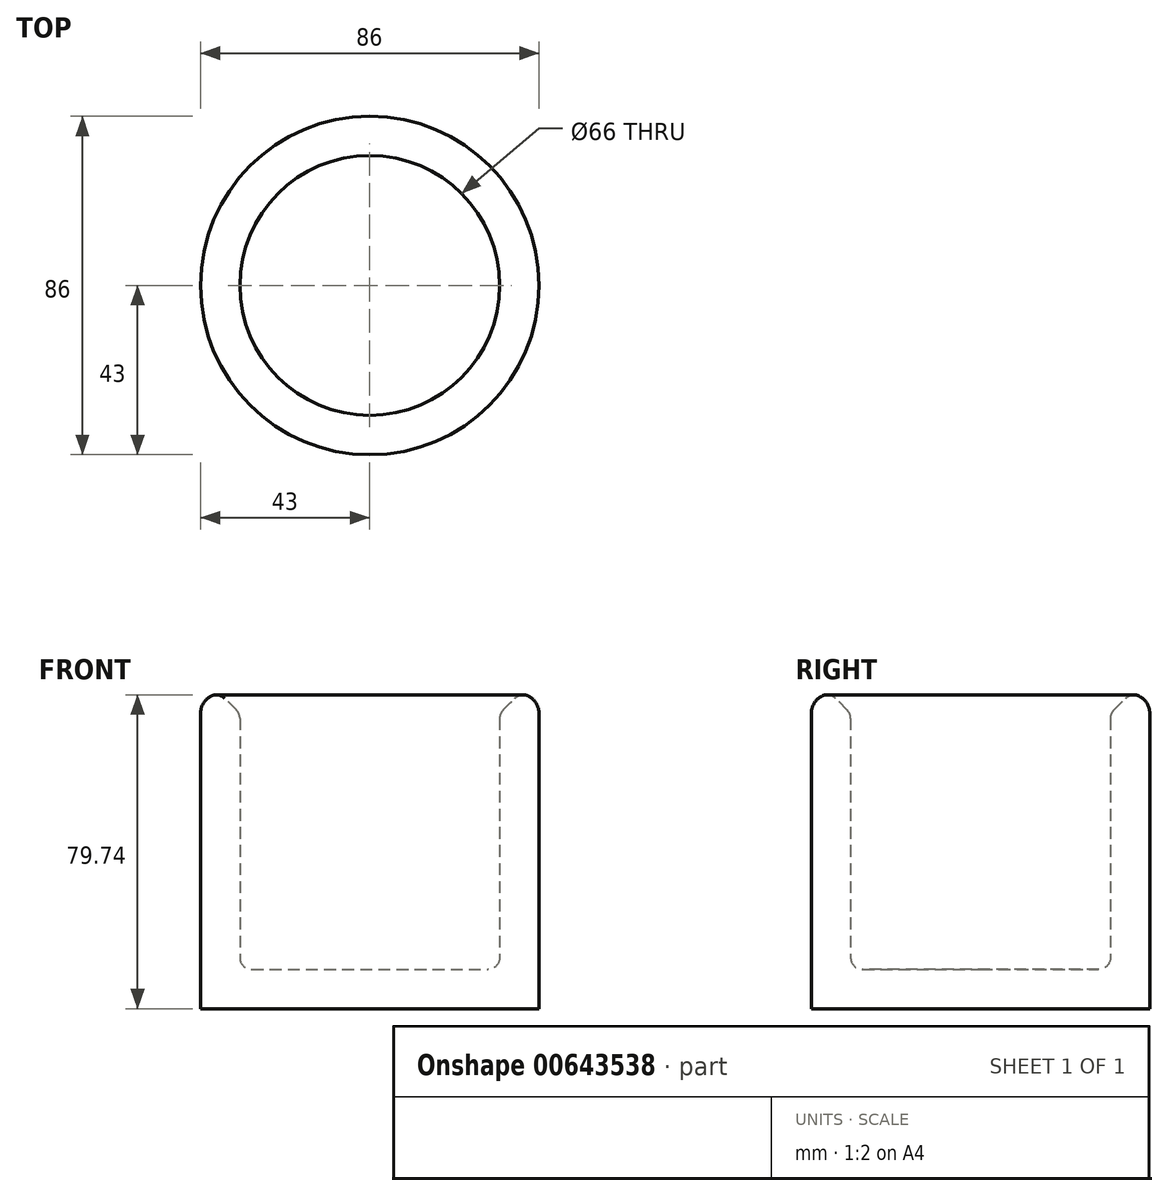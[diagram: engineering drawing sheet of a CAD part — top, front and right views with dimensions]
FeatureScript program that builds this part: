
annotation { "Feature Type Name" : "Feature", "Feature Type Description" : "" }
export const myFeature = defineFeature(function(context is Context, id is Id, definition is map)
    precondition{}
    {
        {
            var Q0;
            Q0=qCreatedBy(makeId("Right.planeOp"),FACE);
            var sketch = newSketch(context, id + "F0", { "sketchPlane" : qUnion([Q0])});
            skLineSegment(sketch, "E0", {"start": v(-43, 80) * mm, "end": v(-43, 0) * mm});
            skLineSegment(sketch, "E1", {"start": v(-43, 0) * mm, "end": v(0, 0) * mm});
            skLineSegment(sketch, "E2", {"start": v(0, 0) * mm, "end": v(0, 10) * mm});
            skLineSegment(sketch, "E3", {"start": v(0, 10) * mm, "end": v(-33, 10) * mm});
            skLineSegment(sketch, "E4", {"start": v(-33, 10) * mm, "end": v(-33, 80) * mm});
            skLineSegment(sketch, "E5", {"start": v(-33, 80) * mm, "end": v(-43, 80) * mm});
            skSolve(sketch);
        }
        {
            var Q0;
            Q0 = qSketchRegion(id + "F0", true);
            var Q1;
            Q1=sQuery(id+"F0.wireOp",EDGE,"E2");
            revolve(context, id + "F1", {"entities" : qUnion([Q0]), "axis" : qUnion([Q1]), "revolveType" : RevolveType.FULL});
        }
        {
            var Q0;
            Q0=makeQuery(id+"F1.opRevolve","SWEPT_EDGE",EDGE,{"disambiguationData":[OSD([sQuery(id+"F0.wireOp",EDGE,"E0"),sQuery(id+"F0.wireOp",EDGE,"E5")])]});
            fillet(context, id + "F2", {"entities" : qUnion([Q0]), "radius" : 5 * mm, "tangentPropagation" : true, "allowEdgeOverflow" : false});
        }
        {
            var Q0;
            Q0=makeQuery(id+"F1.opRevolve","SWEPT_EDGE",EDGE,{"disambiguationData":[OSD([sQuery(id+"F0.wireOp",EDGE,"E4"),sQuery(id+"F0.wireOp",EDGE,"E5")])]});
            chamfer(context, id + "F3", {"entities" : qUnion([Q0]), "width" : 5 * mm, "tangentPropagation" : true});
        }
        {
            var Q0;
            Q0=makeQuery(id+"F1.opRevolve","SWEPT_EDGE",EDGE,{"disambiguationData":[OSD([sQuery(id+"F0.wireOp",EDGE,"E3"),sQuery(id+"F0.wireOp",EDGE,"E4")])]});
            var Q1;
            Q1=makeQuery(id+"F1.opRevolve","SWEPT_FACE",FACE,{"disambiguationData":[OSD([sQuery(id+"F0.wireOp",EDGE,"E3")])]});
            var Q2;
            {var subQ0=sQuery(id+"F0.wireOp",EDGE,"E5");Q2=makeQuery(id+"F3.opChamfer","BLEND_EDGE",EDGE,{"blendedFrom":[makeQuery(id+"F1.opRevolve","SWEPT_EDGE",EDGE,{"disambiguationData":[OSD([sQuery(id+"F0.wireOp",EDGE,"E4"),subQ0])]}),makeQuery(id+"F2.opFillet","BLEND_FACE",FACE,{"disambiguationData":[OSD([sQuery(id+"F0.wireOp",EDGE,"E0"),subQ0])]})],"blendedInto":[makeQuery(id+"F2.opFillet","BLEND_FACE",FACE,{"disambiguationData":[OSD([sQuery(id+"F0.wireOp",EDGE,"E0"),subQ0])]})]});}
            var Q3;
            {var subQ0=sQuery(id+"F0.wireOp",EDGE,"E4");Q3=makeQuery(id+"F3.opChamfer","BLEND_EDGE",EDGE,{"blendedFrom":[makeQuery(id+"F1.opRevolve","SWEPT_EDGE",EDGE,{"disambiguationData":[OSD([subQ0,sQuery(id+"F0.wireOp",EDGE,"E5")])]}),makeQuery(id+"F1.opRevolve","SWEPT_FACE",FACE,{"disambiguationData":[OSD([subQ0])]})],"blendedInto":[makeQuery(id+"F1.opRevolve","SWEPT_FACE",FACE,{"disambiguationData":[OSD([subQ0])]})]});}
            fillet(context, id + "F4", {"entities" : qUnion([Q0, Q1, Q2, Q3]), "radius" : 3 * mm, "tangentPropagation" : true, "allowEdgeOverflow" : false});
        }
    });
